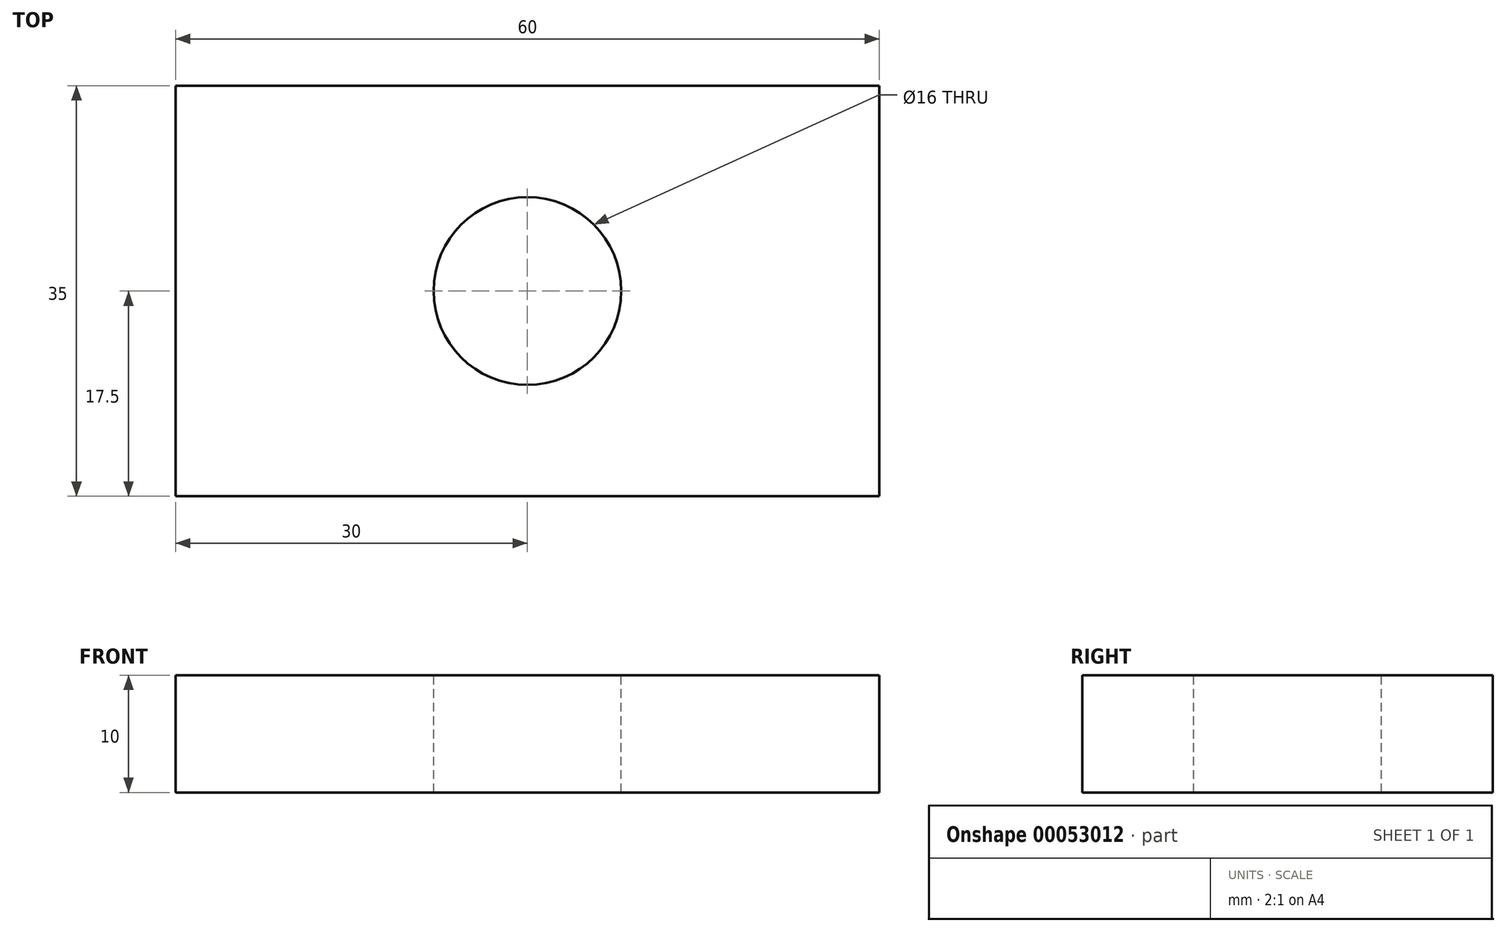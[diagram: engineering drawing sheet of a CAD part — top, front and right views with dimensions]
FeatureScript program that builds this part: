
annotation { "Feature Type Name" : "Feature", "Feature Type Description" : "" }
export const myFeature = defineFeature(function(context is Context, id is Id, definition is map)
    precondition{}
    {
        {
            var Q0;
            Q0=qCreatedBy(makeId("Front.planeOp"),FACE);
            var sketch = newSketch(context, id + "F0", { "sketchPlane" : qUnion([Q0])});
            skLineSegment(sketch, "E0.rect.bottom", {"start": v(30, 5) * mm, "end": v(-30, 5) * mm});
            skLineSegment(sketch, "E0.rect.top", {"start": v(30, -5) * mm, "end": v(-30, -5) * mm});
            skLineSegment(sketch, "E0.rect.left", {"start": v(30, 5) * mm, "end": v(30, -5) * mm});
            skLineSegment(sketch, "E0.rect.right", {"start": v(-30, 5) * mm, "end": v(-30, -5) * mm});
            skPoint(sketch, "E0.rect.middle", {"position": v(0, 0) * mm});
            skSolve(sketch);
        }
        {
            var Q0;
            Q0=makeQuery(id+"F0.imprint","IMPRINT",FACE,{"disambiguationData":[TD([[makeQuery(id+"F0.imprint","IMPRINT",EDGE,{"derivedFrom":sQuery(id+"F0.wireOp",EDGE,"E0.rect.bottom")}),1.0]])]});
            extrude(context, id + "F1", {"entities" : qUnion([Q0]), "endBound" : BoundingType.SYMMETRIC, "depth" : 35 * mm});
        }
        {
            var Q0;
            Q0=makeQuery(id+"F1.opExtrude","SWEPT_FACE",FACE,{"disambiguationData":[OSD([sQuery(id+"F0.wireOp",EDGE,"E0.rect.bottom")])]});
            var sketch = newSketch(context, id + "F2", { "sketchPlane" : qUnion([Q0])});
            skCircle(sketch, "E1", {"center": v(0, 0) * mm, "radius": 8 * mm});
            skSolve(sketch);
        }
        {
            var Q0;
            Q0=qSketchRegion(id+"F2",true);
            var Q1;
            Q1=makeQuery(id+"F2.imprint","IMPRINT",FACE,{"disambiguationData":[TD([[makeQuery(id+"F2.imprint","IMPRINT",EDGE,{"derivedFrom":sQuery(id+"F2.wireOp",EDGE,"E1")}),1.0]])]});
            extrude(context, id + "F3", {"entities" : qUnion([Q0, Q1]), "operationType" : NewBodyOperationType.REMOVE, "endBound" : BoundingType.THROUGH_ALL, "oppositeDirection" : true, "depth" : 25 * mm});
        }
    });
